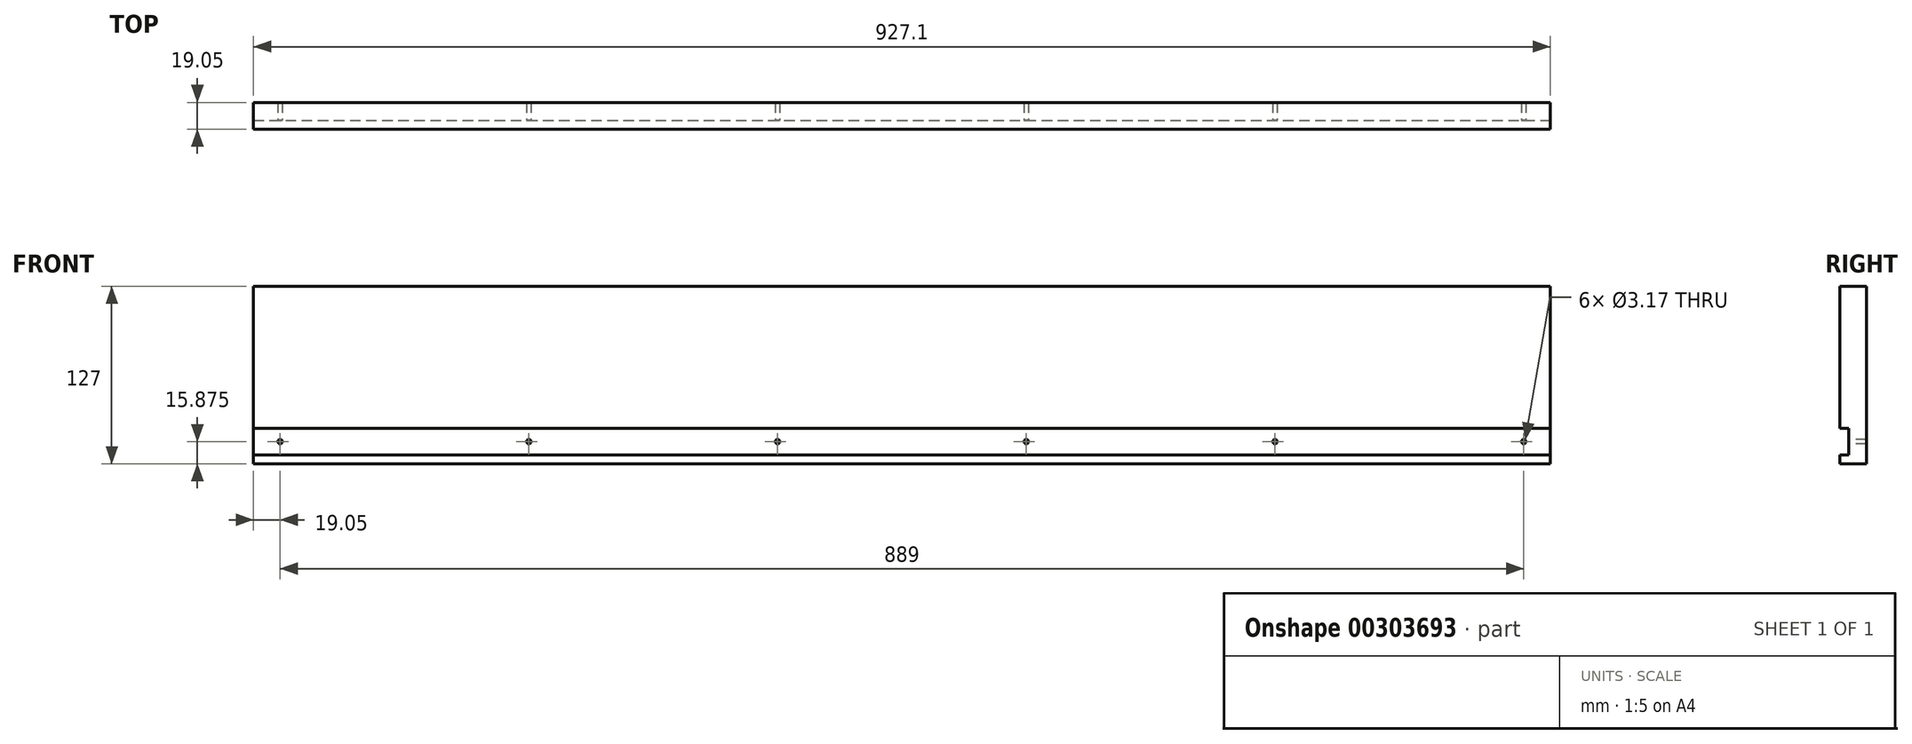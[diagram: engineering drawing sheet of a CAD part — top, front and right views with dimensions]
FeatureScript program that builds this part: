
annotation { "Feature Type Name" : "Feature", "Feature Type Description" : "" }
export const myFeature = defineFeature(function(context is Context, id is Id, definition is map)
    precondition{}
    {
        {
            var Q0;
            Q0=qCreatedBy(makeId("Front.planeOp"),FACE);
            var sketch = newSketch(context, id + "F0", { "sketchPlane" : qUnion([Q0])});
            skLineSegment(sketch, "E0.bottom", {"start": v(0, 0) * mm, "end": v(927.1, 0) * mm});
            skLineSegment(sketch, "E0.top", {"start": v(0, -127) * mm, "end": v(927.1, -127) * mm});
            skLineSegment(sketch, "E0.left", {"start": v(0, 0) * mm, "end": v(0, -127) * mm});
            skLineSegment(sketch, "E0.right", {"start": v(927.1, 0) * mm, "end": v(927.1, -127) * mm});
            skSolve(sketch);
        }
        {
            var Q0;
            Q0 = qSketchRegion(id + "F0", true);
            extrude(context, id + "F1", {"entities" : qUnion([Q0]), "oppositeDirection" : true, "depth" : 19.05 * mm});
        }
        {
            var Q0;
            Q0=qCreatedBy(makeId("Front.planeOp"),FACE);
            var sketch = newSketch(context, id + "F2", { "sketchPlane" : qUnion([Q0])});
            skLineSegment(sketch, "E1.bottom", {"start": v(0, -101.6) * mm, "end": v(927.1, -101.6) * mm});
            skLineSegment(sketch, "E1.top", {"start": v(0, -120.65) * mm, "end": v(927.1, -120.65) * mm});
            skLineSegment(sketch, "E1.left", {"start": v(0, -101.6) * mm, "end": v(0, -120.65) * mm});
            skLineSegment(sketch, "E1.right", {"start": v(927.1, -101.6) * mm, "end": v(927.1, -120.65) * mm});
            skSolve(sketch);
        }
        {
            var Q0;
            Q0 = qSketchRegion(id + "F2", true);
            extrude(context, id + "F3", {"entities" : qUnion([Q0]), "operationType" : NewBodyOperationType.REMOVE, "oppositeDirection" : true, "depth" : 6.35 * mm});
        }
        {
            var Q0;
            Q0=qCreatedBy(makeId("Front.planeOp"),FACE);
            var sketch = newSketch(context, id + "F4", { "sketchPlane" : qUnion([Q0])});
            skCircle(sketch, "E2", {"center": v(19.05, -111.12) * mm, "radius": 1.59 * mm});
            skCircle(sketch, "E3.1.0.0", {"center": v(196.85, -111.12) * mm, "radius": 1.59 * mm});
            skCircle(sketch, "E3.2.0.0", {"center": v(374.65, -111.12) * mm, "radius": 1.59 * mm});
            skCircle(sketch, "E3.3.0.0", {"center": v(552.45, -111.12) * mm, "radius": 1.59 * mm});
            skCircle(sketch, "E3.4.0.0", {"center": v(730.25, -111.12) * mm, "radius": 1.59 * mm});
            skCircle(sketch, "E3.5.0.0", {"center": v(908.05, -111.12) * mm, "radius": 1.59 * mm});
            skLineSegment(sketch, "E3.direction1", {"start": v(19.05, -111.12) * mm, "end": v(196.85, -111.12) * mm, "construction": true});
            skSolve(sketch);
        }
        {
            var Q0;
            Q0 = qSketchRegion(id + "F4", true);
            extrude(context, id + "F5", {"entities" : qUnion([Q0]), "operationType" : NewBodyOperationType.REMOVE, "endBound" : BoundingType.THROUGH_ALL, "oppositeDirection" : true, "depth" : 25.4 * mm});
        }
    });
